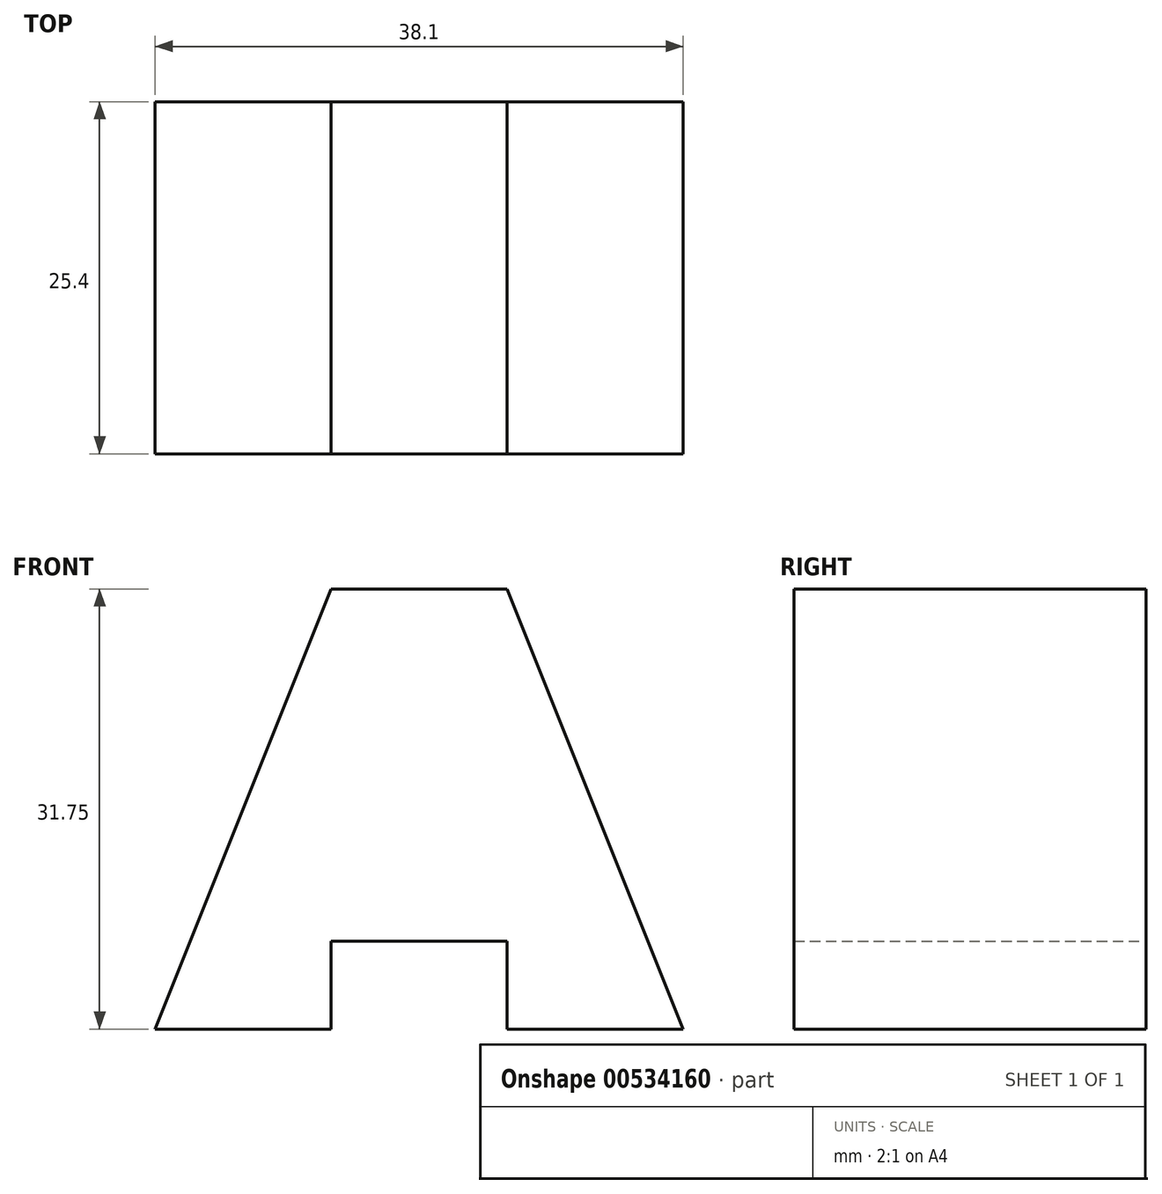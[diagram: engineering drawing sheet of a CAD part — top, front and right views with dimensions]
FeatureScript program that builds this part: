
annotation { "Feature Type Name" : "Feature", "Feature Type Description" : "" }
export const myFeature = defineFeature(function(context is Context, id is Id, definition is map)
    precondition{}
    {
        {
            var Q0;
            Q0=qCreatedBy(makeId("Front.planeOp"),FACE);
            var sketch = newSketch(context, id + "F0", { "sketchPlane" : qUnion([Q0])});
            skLineSegment(sketch, "E0", {"start": v(0, 0) * mm, "end": v(12.7, 0) * mm});
            skLineSegment(sketch, "E1", {"start": v(12.7, 0) * mm, "end": v(12.7, 6.35) * mm});
            skLineSegment(sketch, "E2", {"start": v(12.7, 6.35) * mm, "end": v(25.4, 6.35) * mm});
            skLineSegment(sketch, "E3", {"start": v(25.4, 6.35) * mm, "end": v(25.4, 0) * mm});
            skLineSegment(sketch, "E4", {"start": v(25.4, 0) * mm, "end": v(38.1, 0) * mm});
            skLineSegment(sketch, "E5", {"start": v(25.4, 31.75) * mm, "end": v(38.1, 0) * mm});
            skLineSegment(sketch, "E6", {"start": v(25.4, 31.75) * mm, "end": v(12.7, 31.75) * mm});
            skLineSegment(sketch, "E7", {"start": v(12.7, 31.75) * mm, "end": v(0, 0) * mm});
            skSolve(sketch);
        }
        {
            var Q0;
            Q0=makeQuery(id+"F0.imprint","IMPRINT",FACE,{"disambiguationData":[TD([[makeQuery(id+"F0.imprint","IMPRINT",EDGE,{"derivedFrom":sQuery(id+"F0.wireOp",EDGE,"E0")}),1.0]])]});
            extrude(context, id + "F1", {"entities" : qUnion([Q0]), "depth" : 25.4 * mm, "offsetDistance" : 25.4 * mm});
        }
    });
